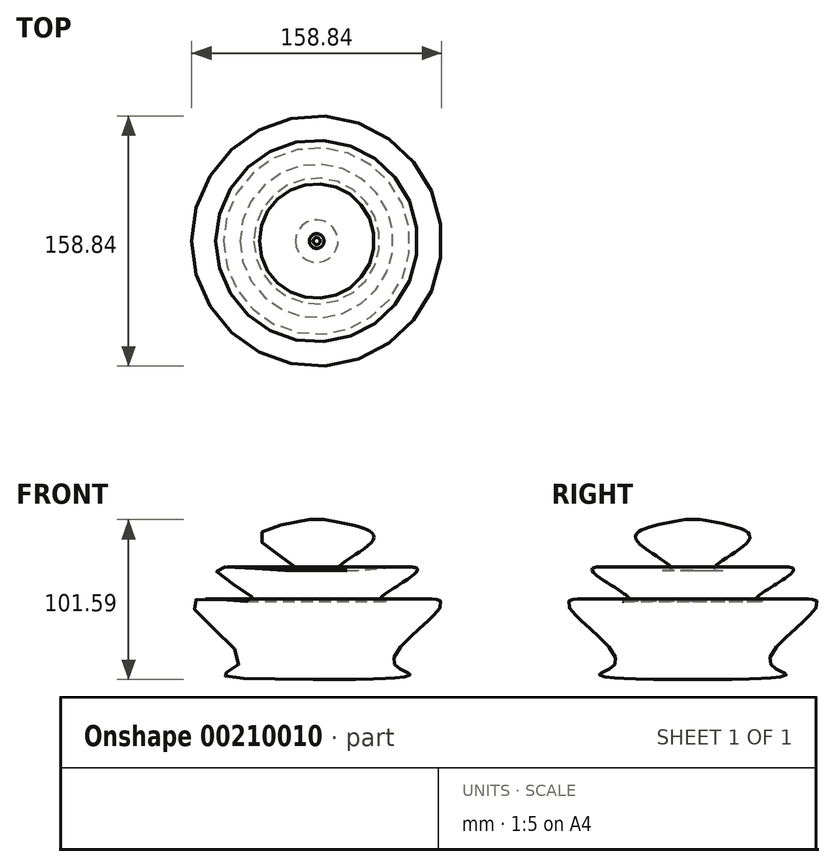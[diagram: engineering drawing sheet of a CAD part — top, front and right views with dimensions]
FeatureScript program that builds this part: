
annotation { "Feature Type Name" : "Feature", "Feature Type Description" : "" }
export const myFeature = defineFeature(function(context is Context, id is Id, definition is map)
    precondition{}
    {
        {
            var Q0;
            Q0=qCreatedBy(makeId("Right.planeOp"),FACE);
            var sketch = newSketch(context, id + "F0", { "sketchPlane" : qUnion([Q0])});
            skFitSpline(sketch, "E0", {"points": [v(4.69, 65.17) * mm, v(35.95, 52.36) * mm, v(13.75, 33.6) * mm, v(64.08, 33.6) * mm, v(40.01, 14.22) * mm, v(79.08, 12.97) * mm, v(48.76, -23.91) * mm, v(59.08, -32.98) * mm, v(2.19, -36.42) * mm], "startDerivative": vector(434.68, -74.25) * mm, "endDerivative": vector(-572.56, -3.75) * mm});
            skLineSegment(sketch, "E1", {"start": v(0, 72.05) * mm, "end": v(0, 94.87) * mm});
            skLineSegment(sketch, "E2", {"start": v(0, 94.87) * mm, "end": v(0, 72.05) * mm});
            skSolve(sketch);
        }
        {
            var Q0;
            Q0=sQuery(id+"F0.wireOp",EDGE,"E0");
            var Q1;
            Q1=sQuery(id+"F0.wireOp",EDGE,"E2");
            revolve(context, id + "F1", {"bodyType" : ToolBodyType.SURFACE, "surfaceEntities" : qUnion([Q0]), "axis" : qUnion([Q1]), "revolveType" : RevolveType.FULL});
        }
    });
